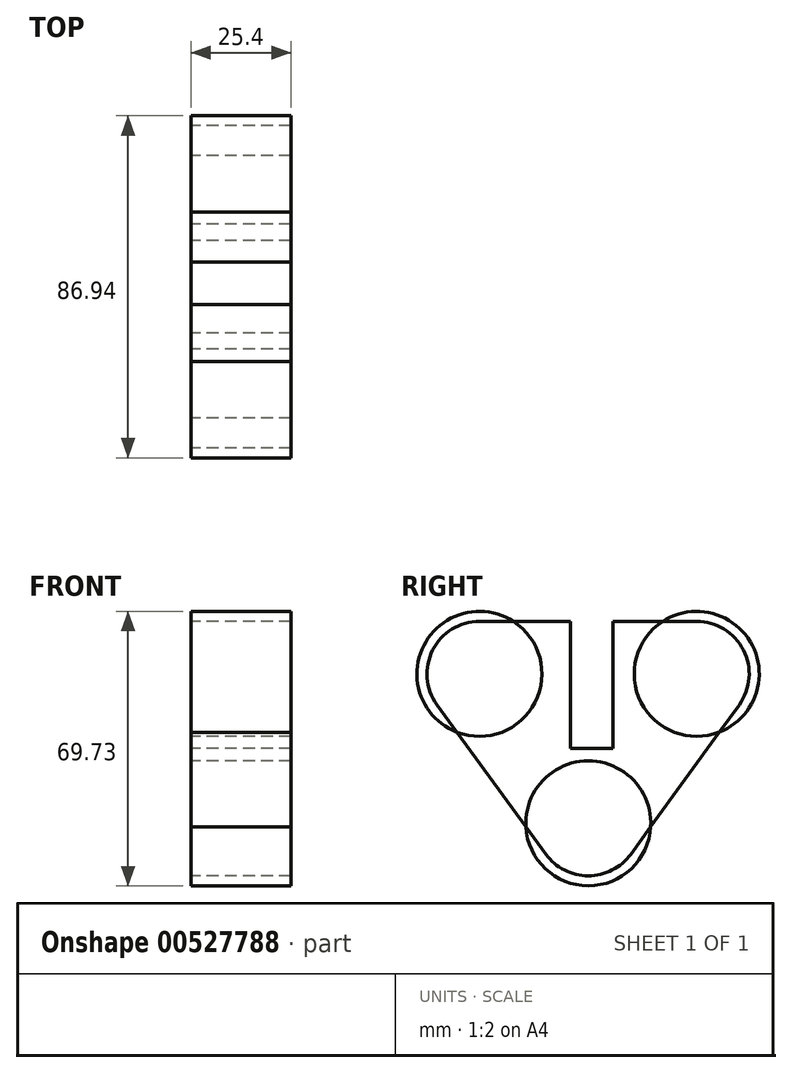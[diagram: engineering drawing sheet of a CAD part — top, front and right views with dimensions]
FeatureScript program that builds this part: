
annotation { "Feature Type Name" : "Feature", "Feature Type Description" : "" }
export const myFeature = defineFeature(function(context is Context, id is Id, definition is map)
    precondition{}
    {
        {
            var Q0;
            Q0=qCreatedBy(makeId("Right.planeOp"),FACE);
            var sketch = newSketch(context, id + "F0", { "sketchPlane" : qUnion([Q0])});
            skCircle(sketch, "E0", {"center": v(-27.65, 0) * mm, "radius": 13.34 * mm});
            skCircle(sketch, "E1", {"center": v(27.55, 0) * mm, "radius": 13.34 * mm});
            skCircle(sketch, "E2", {"center": v(0, -37.97) * mm, "radius": 13.34 * mm});
            skLineSegment(sketch, "E3", {"start": v(-27.65, 13.34) * mm, "end": v(27.55, 13.34) * mm});
            skLineSegment(sketch, "E4", {"start": v(-38.43, -7.85) * mm, "end": v(-10.78, -45.82) * mm});
            skLineSegment(sketch, "E5", {"start": v(38.34, -7.83) * mm, "end": v(10.8, -45.8) * mm});
            skLineSegment(sketch, "E6", {"start": v(-0.05, 13.33) * mm, "end": v(-0.05, -51.3) * mm, "construction": true});
            skPoint(sketch, "E7.oppositeSnap0", {"position": v(-0.05, -18.99) * mm});
            skLineSegment(sketch, "E7.top", {"start": v(6.28, -18.99) * mm, "end": v(-4.57, -18.99) * mm});
            skLineSegment(sketch, "E7.left", {"start": v(6.28, 13.33) * mm, "end": v(6.28, -18.99) * mm});
            skLineSegment(sketch, "E7.right", {"start": v(-4.57, 13.33) * mm, "end": v(-4.57, -18.99) * mm});
            skPoint(sketch, "E8", {"position": v(24.57, -26.82) * mm});
            skPoint(sketch, "E9", {"position": v(-24.6, -26.84) * mm});
            skCircle(sketch, "E10", {"center": v(27.55, 0) * mm, "radius": 15.88 * mm});
            skCircle(sketch, "E11", {"center": v(0, -37.97) * mm, "radius": 15.88 * mm});
            skCircle(sketch, "E12", {"center": v(-27.65, 0) * mm, "radius": 15.88 * mm});
            skSolve(sketch);
        }
        {
            var Q0;
            Q0=makeQuery(id+"F0.imprint","IMPRINT",FACE,{"disambiguationData":[TD([[makeQuery(id+"F0.imprint","IMPRINT",EDGE,{"derivedFrom":sQuery(id+"F0.wireOp",EDGE,"E7.top")}),1.0]])]});
            var Q1;
            {var subQ0=sQuery(id+"F0.wireOp",EDGE,"E4");var subQ1=sQuery(id+"F0.wireOp",EDGE,"E2");var subQ2=makeQuery(id+"F0.imprint","INTERSECT",VERTEX,{"derivedFrom":[subQ1,subQ0]});Q1=makeQuery(id+"F0.imprint","IMPRINT",FACE,{"disambiguationData":[TD([[makeQuery(id+"F0.imprint","IMPRINT",EDGE,{"disambiguationData":[TD([[subQ2,-1.0]])],"derivedFrom":subQ1}),-1.0]])]});}
            var Q2;
            {var subQ0=sQuery(id+"F0.wireOp",EDGE,"E3");var subQ1=sQuery(id+"F0.wireOp",EDGE,"E0");var subQ2=makeQuery(id+"F0.imprint","INTERSECT",VERTEX,{"derivedFrom":[subQ1,subQ0]});Q2=makeQuery(id+"F0.imprint","IMPRINT",FACE,{"disambiguationData":[TD([[makeQuery(id+"F0.imprint","IMPRINT",EDGE,{"disambiguationData":[TD([[subQ2,-1.0]])],"derivedFrom":subQ1}),-1.0]])]});}
            var Q3;
            {var subQ0=sQuery(id+"F0.wireOp",EDGE,"E3");var subQ1=sQuery(id+"F0.wireOp",EDGE,"E1");var subQ2=makeQuery(id+"F0.imprint","INTERSECT",VERTEX,{"derivedFrom":[subQ1,subQ0]});Q3=makeQuery(id+"F0.imprint","IMPRINT",FACE,{"disambiguationData":[TD([[makeQuery(id+"F0.imprint","IMPRINT",EDGE,{"disambiguationData":[TD([[subQ2,1.0]])],"derivedFrom":subQ1}),-1.0]])]});}
            extrude(context, id + "F1", {"entities" : qUnion([Q0, Q1, Q2, Q3]), "depth" : 25.4 * mm, "offsetDistance" : 25.4 * mm});
        }
    });
